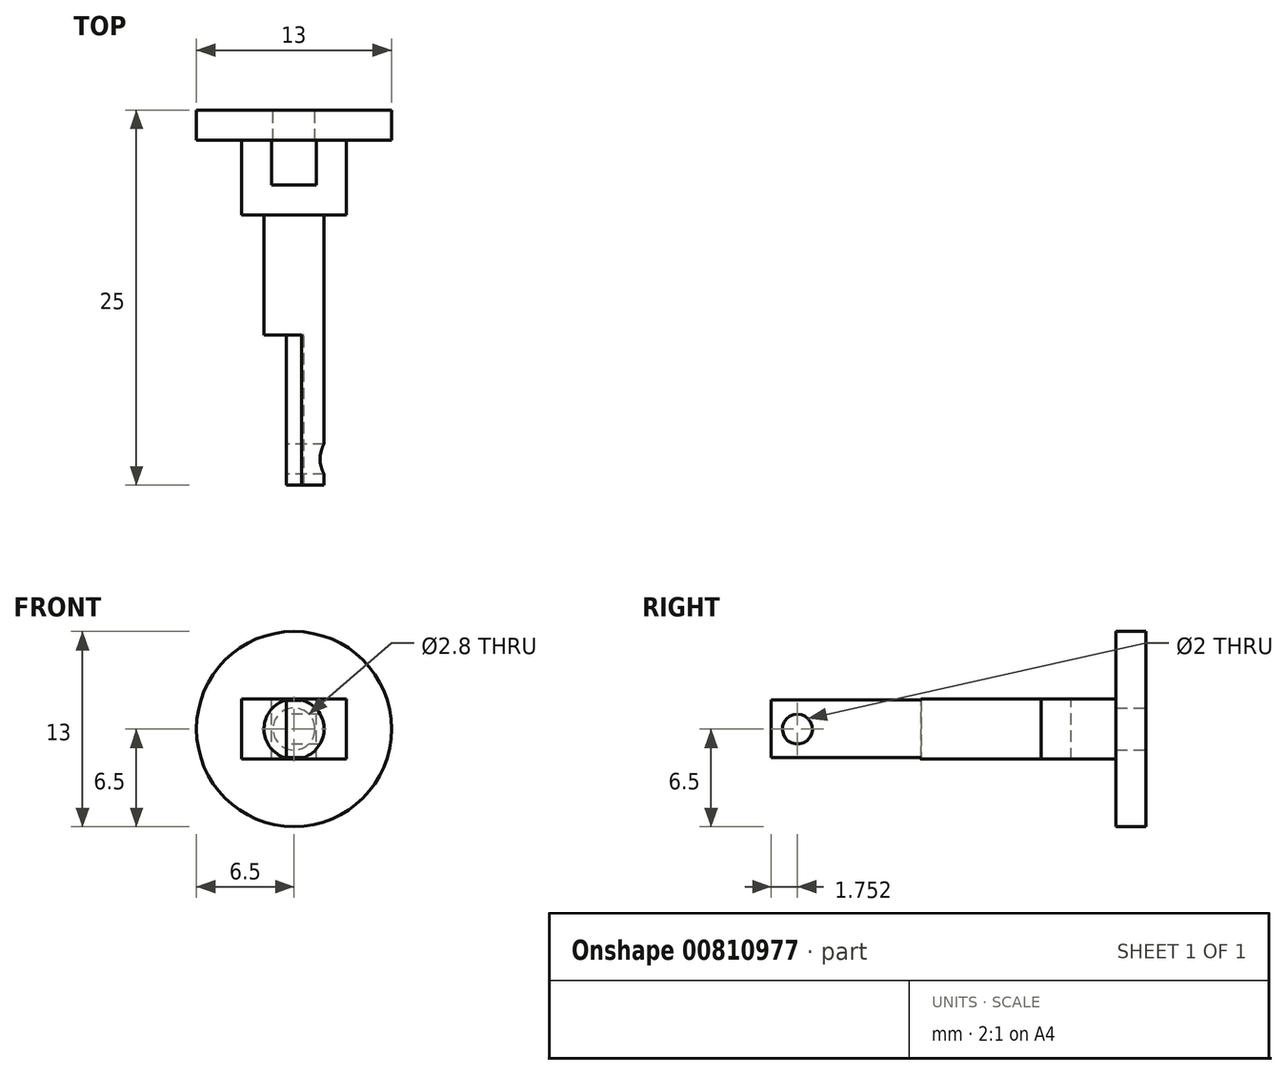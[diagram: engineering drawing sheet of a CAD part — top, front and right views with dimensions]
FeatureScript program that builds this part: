
annotation { "Feature Type Name" : "Feature", "Feature Type Description" : "" }
export const myFeature = defineFeature(function(context is Context, id is Id, definition is map)
    precondition{}
    {
        {
            var Q0;
            Q0=qCreatedBy(makeId("Front.planeOp"),FACE);
            var sketch = newSketch(context, id + "F0", { "sketchPlane" : qUnion([Q0])});
            skCircle(sketch, "E0", {"center": v(0, 0) * mm, "radius": 6.5 * mm});
            skCircle(sketch, "E1", {"center": v(0, 0) * mm, "radius": 1.4 * mm});
            skLineSegment(sketch, "E2.bottom", {"start": v(-3.5, -2) * mm, "end": v(-1.5, -2) * mm});
            skLineSegment(sketch, "E2.top", {"start": v(-3.5, 2) * mm, "end": v(-1.5, 2) * mm});
            skLineSegment(sketch, "E2.left", {"start": v(-3.5, -2) * mm, "end": v(-3.5, 2) * mm});
            skLineSegment(sketch, "E2.right", {"start": v(-1.5, -2) * mm, "end": v(-1.5, 2) * mm});
            skPoint(sketch, "E2.middle", {"position": v(-2.5, 0) * mm});
            skLineSegment(sketch, "E3.bottom", {"start": v(3.5, -2) * mm, "end": v(1.5, -2) * mm});
            skLineSegment(sketch, "E3.top", {"start": v(3.5, 2) * mm, "end": v(1.5, 2) * mm});
            skLineSegment(sketch, "E3.left", {"start": v(3.5, -2) * mm, "end": v(3.5, 2) * mm});
            skLineSegment(sketch, "E3.right", {"start": v(1.5, -2) * mm, "end": v(1.5, 2) * mm});
            skPoint(sketch, "E3.middle", {"position": v(2.5, 0) * mm});
            skSolve(sketch);
        }
        {
            var Q0;
            Q0=makeQuery(id+"F0.imprint","IMPRINT",FACE,{"disambiguationData":[TD([[makeQuery(id+"F0.imprint","IMPRINT",EDGE,{"derivedFrom":sQuery(id+"F0.wireOp",EDGE,"E0")}),1.0]])]});
            extrude(context, id + "F1", {"entities" : qUnion([Q0]), "depth" : 2 * mm, "offsetDistance" : 25 * mm});
        }
        {
            var Q0;
            Q0=makeQuery(id+"F0.imprint","IMPRINT",FACE,{"disambiguationData":[TD([[makeQuery(id+"F0.imprint","IMPRINT",EDGE,{"derivedFrom":sQuery(id+"F0.wireOp",EDGE,"E2.bottom")}),1.0]])]});
            var Q1;
            Q1=makeQuery(id+"F0.imprint","IMPRINT",FACE,{"disambiguationData":[TD([[makeQuery(id+"F0.imprint","IMPRINT",EDGE,{"derivedFrom":sQuery(id+"F0.wireOp",EDGE,"E3.bottom")}),-1.0]])]});
            extrude(context, id + "F2", {"entities" : qUnion([Q0, Q1]), "operationType" : NewBodyOperationType.ADD, "depth" : 5 * mm, "offsetDistance" : 25 * mm});
        }
        {
            var Q0;
            Q0=makeQuery(id+"F2.opExtrude","CAP_FACE",FACE,{"disambiguationData":[OSD([sQuery(id+"F0.wireOp",EDGE,"E3.bottom"),sQuery(id+"F0.wireOp",EDGE,"E3.top"),sQuery(id+"F0.wireOp",EDGE,"E3.left"),sQuery(id+"F0.wireOp",EDGE,"E3.right")])],"isStart":false});
            var sketch = newSketch(context, id + "F3", { "sketchPlane" : qUnion([Q0])});
            skLineSegment(sketch, "E4.bottom", {"start": v(3.5, -2) * mm, "end": v(-3.5, -2) * mm});
            skLineSegment(sketch, "E4.top", {"start": v(3.5, 2) * mm, "end": v(-3.5, 2) * mm});
            skLineSegment(sketch, "E4.left", {"start": v(3.5, -2) * mm, "end": v(3.5, 2) * mm});
            skLineSegment(sketch, "E4.right", {"start": v(-3.5, -2) * mm, "end": v(-3.5, 2) * mm});
            skSolve(sketch);
        }
        {
            var Q0;
            Q0 = qSketchRegion(id + "F3", true);
            extrude(context, id + "F4", {"entities" : qUnion([Q0]), "operationType" : NewBodyOperationType.ADD, "depth" : 2 * mm, "offsetDistance" : 25 * mm});
        }
        {
            var Q0;
            Q0=makeQuery(id+"F4.opExtrude","CAP_FACE",FACE,{"disambiguationData":[OSD([sQuery(id+"F3.wireOp",EDGE,"E4.bottom"),sQuery(id+"F3.wireOp",EDGE,"E4.top"),sQuery(id+"F3.wireOp",EDGE,"E4.left"),sQuery(id+"F3.wireOp",EDGE,"E4.right")])],"isStart":false});
            var sketch = newSketch(context, id + "F5", { "sketchPlane" : qUnion([Q0])});
            skCircle(sketch, "E5", {"center": v(0, 0) * mm, "radius": 2 * mm});
            skSolve(sketch);
        }
        {
            var Q0;
            Q0 = qSketchRegion(id + "F5", true);
            extrude(context, id + "F6", {"entities" : qUnion([Q0]), "operationType" : NewBodyOperationType.ADD, "depth" : 8 * mm, "offsetDistance" : 25 * mm});
        }
        {
            var Q0;
            Q0=makeQuery(id+"F6.opExtrude","CAP_FACE",FACE,{"disambiguationData":[OSD([sQuery(id+"F5.wireOp",EDGE,"E5")])],"isStart":false});
            var sketch = newSketch(context, id + "F7", { "sketchPlane" : qUnion([Q0])});
            skLineSegment(sketch, "E6.bottom", {"start": v(0.5, -1.9) * mm, "end": v(-0.5, -1.9) * mm});
            skLineSegment(sketch, "E6.top", {"start": v(0.5, 1.9) * mm, "end": v(-0.5, 1.9) * mm});
            skLineSegment(sketch, "E6.left", {"start": v(0.5, -1.9) * mm, "end": v(0.5, 1.9) * mm});
            skLineSegment(sketch, "E6.right", {"start": v(-0.5, -1.9) * mm, "end": v(-0.5, 1.9) * mm});
            skPoint(sketch, "E6.middle", {"position": v(0, 0) * mm});
            skLineSegment(sketch, "E7", {"start": v(0.67, -1.89) * mm, "end": v(0.5, -1.9) * mm});
            skLineSegment(sketch, "E8", {"start": v(0.5, 1.9) * mm, "end": v(0.5, 1.94) * mm});
            skSolve(sketch);
        }
        {
            var Q0;
            Q0=makeQuery(id+"F7.imprint","IMPRINT",FACE,{"disambiguationData":[TD([[makeQuery(id+"F7.imprint","IMPRINT",EDGE,{"derivedFrom":sQuery(id+"F7.wireOp",EDGE,"E6.bottom")}),-1.0]])]});
            extrude(context, id + "F8", {"entities" : qUnion([Q0]), "operationType" : NewBodyOperationType.ADD, "depth" : 10 * mm, "offsetDistance" : 25 * mm});
        }
        {
            var Q0;
            Q0=makeQuery(id+"F8.opExtrude","SWEPT_FACE",FACE,{"disambiguationData":[OSD([sQuery(id+"F7.wireOp",EDGE,"E6.right")])]});
            var sketch = newSketch(context, id + "F9", { "sketchPlane" : qUnion([Q0])});
            skCircle(sketch, "E9", {"center": v(23.25, 0) * mm, "radius": 1 * mm});
            skSolve(sketch);
        }
        {
            var Q0;
            Q0=makeQuery(id+"F9.imprint","IMPRINT",FACE,{"disambiguationData":[TD([[makeQuery(id+"F9.imprint","IMPRINT",EDGE,{"derivedFrom":sQuery(id+"F9.wireOp",EDGE,"E9")}),1.0]])]});
            extrude(context, id + "F10", {"entities" : qUnion([Q0]), "operationType" : NewBodyOperationType.REMOVE, "oppositeDirection" : true, "depth" : 3.46 * mm, "offsetDistance" : 25 * mm});
        }
        {
            var Q0;
            Q0=makeQuery(id+"F7.imprint","IMPRINT",FACE,{"disambiguationData":[TD([[makeQuery(id+"F7.imprint","IMPRINT",EDGE,{"derivedFrom":sQuery(id+"F7.wireOp",EDGE,"E6.left")}),-1.0]])]});
            extrude(context, id + "F11", {"entities" : qUnion([Q0]), "operationType" : NewBodyOperationType.ADD, "depth" : 10 * mm, "offsetDistance" : 25 * mm});
        }
        {
            var Q0;
            Q0=makeQuery(id+"F11.boolean.opBoolean","SPLIT",FACE,{"disambiguationData":[TD([makeQuery(id+"F10.boolean.opBoolean","COPY",FACE,{"derivedFrom":makeQuery(id+"F10.opExtrude","SWEPT_FACE",FACE,{"disambiguationData":[OSD([sQuery(id+"F9.wireOp",EDGE,"E9")])]})})])],"derivedFrom":makeQuery(id+"F11.opExtrude","SWEPT_FACE",FACE,{"disambiguationData":[OSD([sQuery(id+"F7.wireOp",EDGE,"E6.left"),sQuery(id+"F7.wireOp",EDGE,"E8")])]})});
            extrude(context, id + "F12", {"entities" : qUnion([Q0]), "operationType" : NewBodyOperationType.REMOVE, "oppositeDirection" : true, "depth" : 2.95 * mm, "offsetDistance" : 25 * mm});
        }
    });
